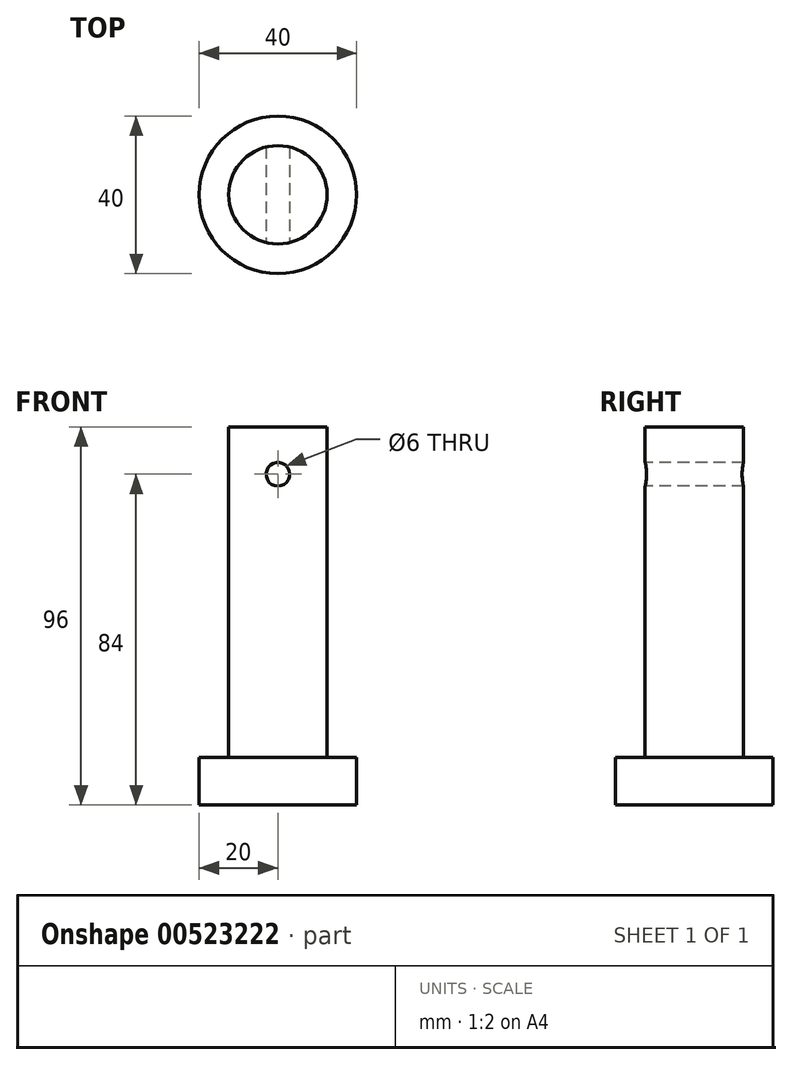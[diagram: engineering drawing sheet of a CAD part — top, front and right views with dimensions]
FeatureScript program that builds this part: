
annotation { "Feature Type Name" : "Feature", "Feature Type Description" : "" }
export const myFeature = defineFeature(function(context is Context, id is Id, definition is map)
    precondition{}
    {
        {
            var Q0;
            Q0=qCreatedBy(makeId("Top.planeOp"),FACE);
            var sketch = newSketch(context, id + "F0", { "sketchPlane" : qUnion([Q0])});
            skCircle(sketch, "E0", {"center": v(0, 0) * mm, "radius": 20 * mm});
            skSolve(sketch);
        }
        {
            var Q0;
            Q0 = qSketchRegion(id + "F0", true);
            extrude(context, id + "F1", {"entities" : qUnion([Q0]), "depth" : 12 * mm, "offsetDistance" : 25 * mm});
        }
        {
            var Q0;
            Q0=makeQuery(id+"F1.opExtrude","CAP_FACE",FACE,{"disambiguationData":[OSD([sQuery(id+"F0.wireOp",EDGE,"E0")])],"isStart":false});
            var sketch = newSketch(context, id + "F2", { "sketchPlane" : qUnion([Q0])});
            skCircle(sketch, "E1", {"center": v(0, 0) * mm, "radius": 12.5 * mm});
            skSolve(sketch);
        }
        {
            var Q0;
            Q0 = qSketchRegion(id + "F2", true);
            extrude(context, id + "F3", {"entities" : qUnion([Q0]), "operationType" : NewBodyOperationType.ADD, "depth" : 84 * mm, "offsetDistance" : 25 * mm});
        }
        {
            var Q0;
            Q0=qCreatedBy(makeId("Front.planeOp"),FACE);
            var sketch = newSketch(context, id + "F4", { "sketchPlane" : qUnion([Q0])});
            skCircle(sketch, "E2", {"center": v(0, 84) * mm, "radius": 3 * mm});
            skSolve(sketch);
        }
        {
            var Q0;
            Q0 = qSketchRegion(id + "F4", true);
            extrude(context, id + "F5", {"entities" : qUnion([Q0]), "operationType" : NewBodyOperationType.REMOVE, "endBound" : BoundingType.SYMMETRIC, "oppositeDirection" : true, "depth" : 50 * mm, "offsetDistance" : 25 * mm});
        }
    });
